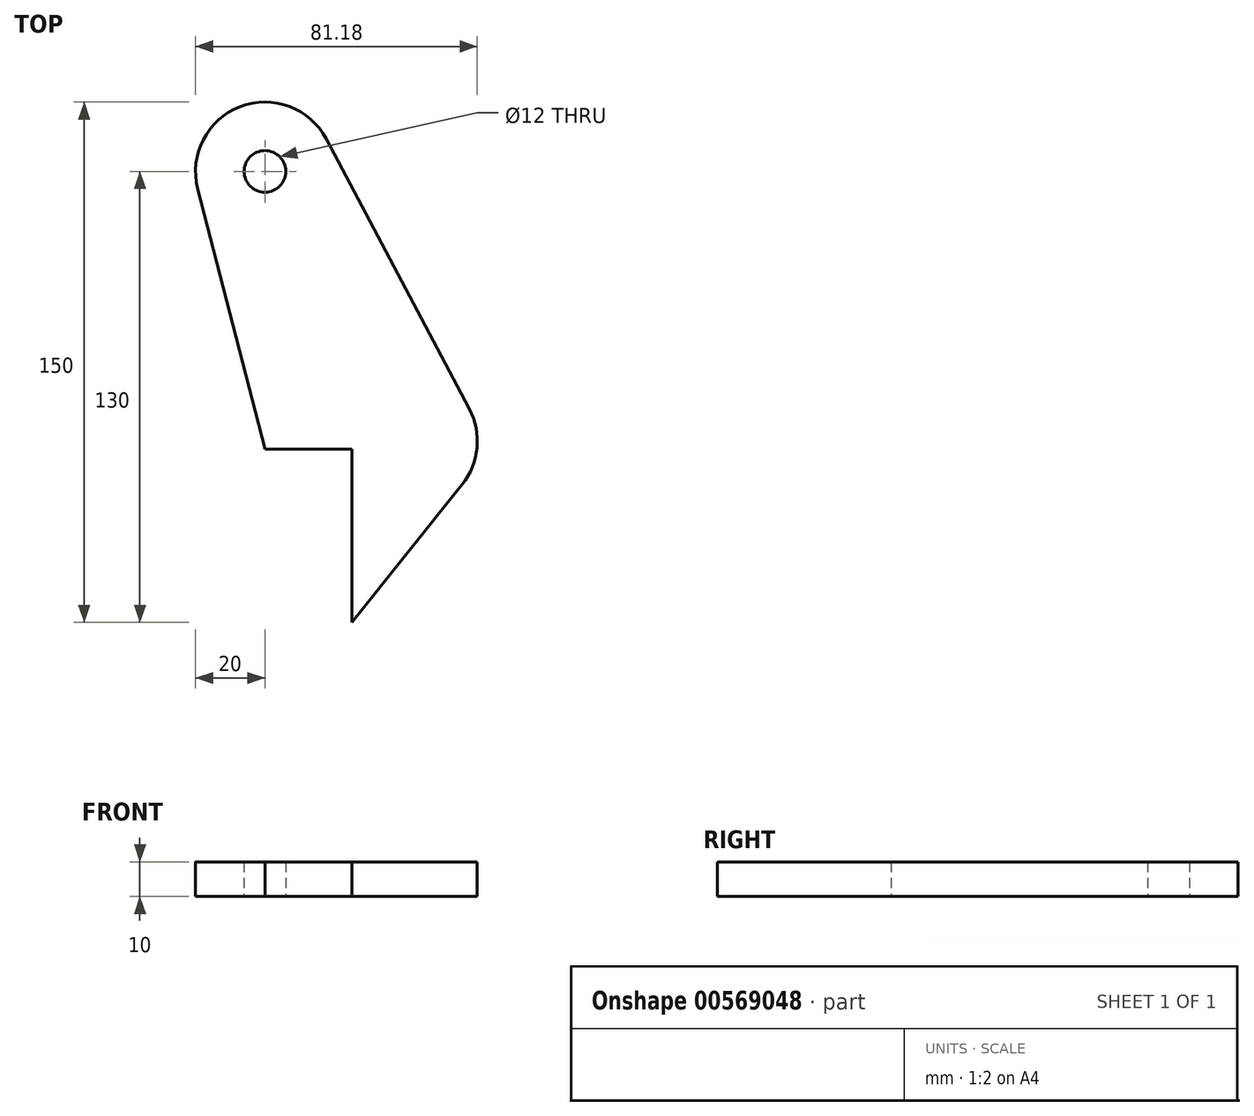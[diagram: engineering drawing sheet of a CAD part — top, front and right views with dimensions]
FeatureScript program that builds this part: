
annotation { "Feature Type Name" : "Feature", "Feature Type Description" : "" }
export const myFeature = defineFeature(function(context is Context, id is Id, definition is map)
    precondition{}
    {
        {
            var Q0;
            Q0=qCreatedBy(makeId("Top.planeOp"), FACE);
            var sketch = newSketch(context, id + "F0", { "sketchPlane" : qUnion([Q0])});
            skCircle(sketch, "E0", {"center": v(0, 0) * mm, "radius": 6 * mm});
            skArc(sketch, "E1", {"start": v(17.67, 9.36) * mm, "mid": v(-7.23, 18.65) * mm, "end": v(-19.36, -5) * mm});
            skLineSegment(sketch, "E2", {"start": v(0, -80) * mm, "end": v(-19.36, -5) * mm});
            skLineSegment(sketch, "E3", {"start": v(0, -80) * mm, "end": v(25, -80) * mm});
            skLineSegment(sketch, "E4", {"start": v(25, -80) * mm, "end": v(25, -130) * mm});
            skLineSegment(sketch, "E5", {"start": v(25, -130) * mm, "end": v(56.8, -90.25) * mm});
            skLineSegment(sketch, "E6", {"start": v(58.86, -68.4) * mm, "end": v(17.67, 9.36) * mm});
            skPoint(sketch, "E7.visualSharp", {"position": v(65, -80) * mm});
            skArc(sketch, "E7.filletArc", {"start": v(56.8, -90.25) * mm, "mid": v(61.1, -79.63) * mm, "end": v(58.86, -68.4) * mm});
            skSolve(sketch);
        }
        {
            var Q0;
            Q0 = qSketchRegion(id + "F0", true);
            extrude(context, id + "F1", {"entities" : qUnion([Q0]), "depth" : 10 * mm, "offsetDistance" : 25 * mm});
        }
    });
